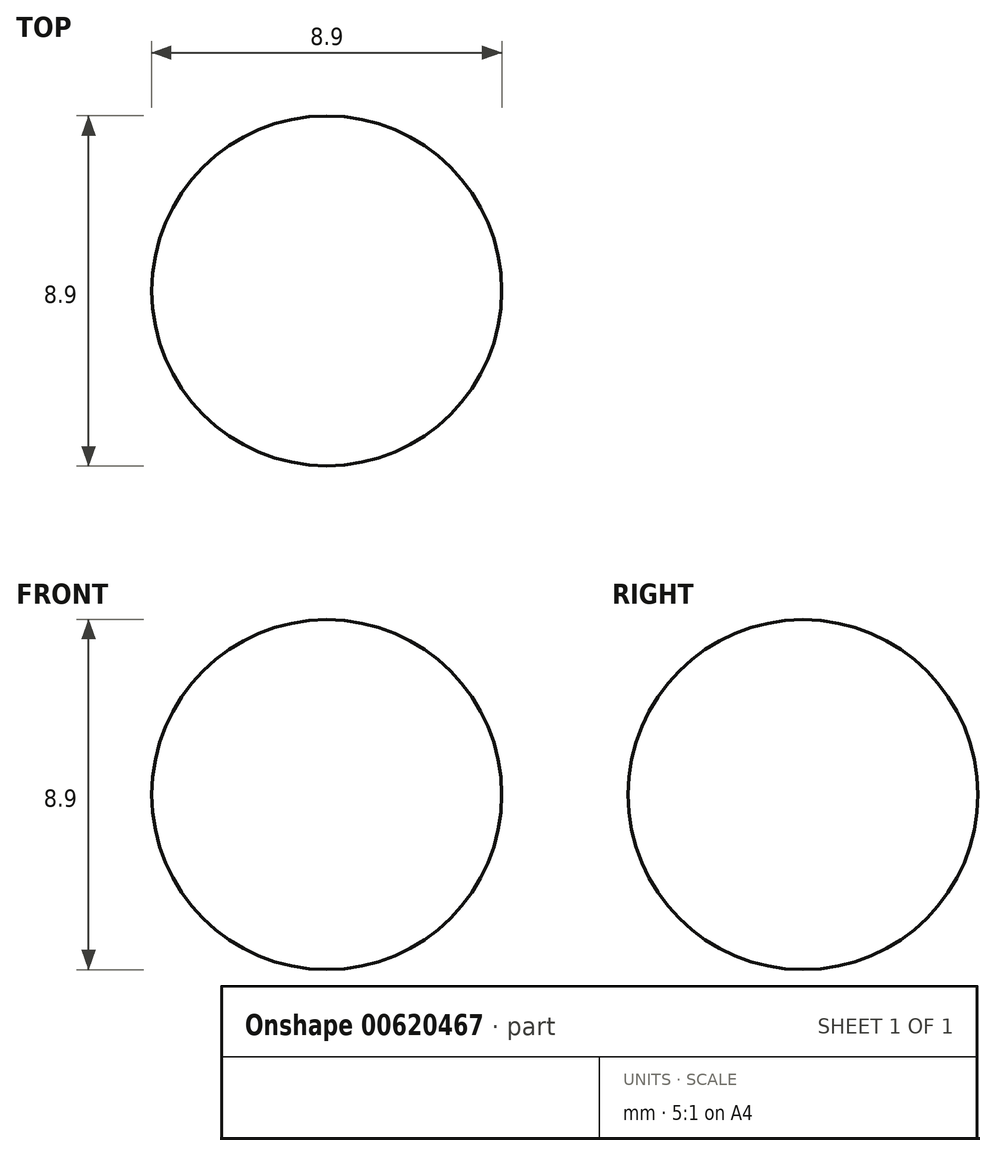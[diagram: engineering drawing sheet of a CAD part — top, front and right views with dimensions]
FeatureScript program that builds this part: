
annotation { "Feature Type Name" : "Feature", "Feature Type Description" : "" }
export const myFeature = defineFeature(function(context is Context, id is Id, definition is map)
    precondition{}
    {
        {
            var Q0;
            Q0=qCreatedBy(makeId("Front.planeOp"),FACE);
            var sketch = newSketch(context, id + "F0", { "sketchPlane" : qUnion([Q0])});
            skCircle(sketch, "E0", {"center": v(0, 0) * mm, "radius": 4.45 * mm});
            skLineSegment(sketch, "E1", {"start": v(-6.3, 0) * mm, "end": v(8.07, 0) * mm});
            skSolve(sketch);
        }
        {
            var Q0;
            {var subQ0=sQuery(id+"F0.wireOp",EDGE,"E1");var subQ1=sQuery(id+"F0.wireOp",EDGE,"E0");var subQ2=makeQuery(id+"F0.imprint","INTERSECT",VERTEX,{"disambiguationData":[OD(0.0)],"derivedFrom":[subQ1,subQ0]});Q0=makeQuery(id+"F0.imprint","IMPRINT",FACE,{"disambiguationData":[TD([[makeQuery(id+"F0.imprint","IMPRINT",EDGE,{"disambiguationData":[TD([[subQ2,-1.0]])],"derivedFrom":subQ1}),1.0]])]});}
            var Q1;
            Q1=sQuery(id+"F0.wireOp",EDGE,"E1");
            revolve(context, id + "F1", {"entities" : qUnion([Q0]), "axis" : qUnion([Q1]), "revolveType" : RevolveType.FULL});
        }
    });
